# Revit family: Basketball_Backstop-Wall_Mount-Stationary-IPIbyBison-PKGxxSTRG
name_source: partatom
category: Specialty Equipment
units: mm (PartAtom-declared; Revit-internal decimal feet)

## family parameters
Always vertical = Yes
Cut with Voids When Loaded = No
Enable Cutting in Views = No
Maintain Annotation Orientation = No
OmniClass Number = 23.40.50.34.14
OmniClass Title = Gymnasium Equipment
Part Type = Normal
Room Calculation Point = No
Round Connector Dimension = Use Diameter
Shared = No
Work Plane-Based = No

## types (3) — shared parameters
Backboard Frame Material = Steel - IPI by Bison - Tubular Support
Backboard Height = 3' - 6"
Backboard Material = Fiberglass - IPI by Bison - Backboard
CAD Details = https://www.arcat.com
Default Elevation = 0' - 0"
Description = Basketball Frame and Backboard, Wall Mount
Hoop Finish = Powder Coat - IPI by Bison - Outdoor Orange
Keynote = 11 66 00
Manufacturer = IPI by Bison
Netting = Finish - IPI by Bison - White Netting
PKG46STRG Extension Range = 48" to 72"
PKG68STRG Extension Range = 72" to 96"
PKG82STRG Extension Range = 96" to 144"
Product Page URL = https://www.arcat.com
Specification = https://www.arcat.com
Support Tubing Diameter = 0' - 1 29/32"
Support Tubing Material = Steel - IPI by Bison - Tubular Support
Suspension Type = Telescoping
URL = https://ipibybison.com
Wall Plate Material = Wood - IPI by Bison
Width = 6' - 0"

## per-type parameters (varying)
| type | Extension Depth |
| PKG68STRG | 6' - 0" |
| PKG82STRG | 8' - 0" |
| PKG46STRG | 4' - 0" |

note: column(s) folded — value = type name in every type: Model

## geometry (parser evidence)
native form markers: Sweep x5
no freeform markers — native parametric forms only
